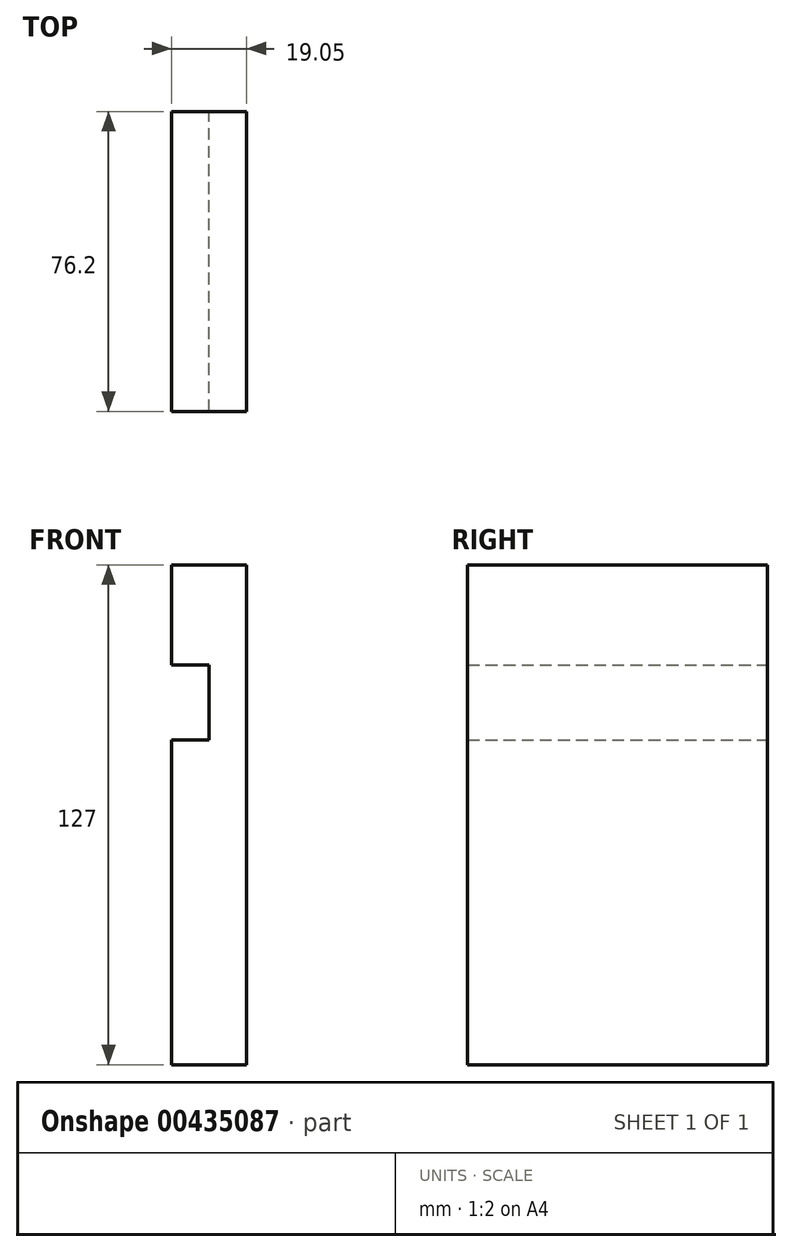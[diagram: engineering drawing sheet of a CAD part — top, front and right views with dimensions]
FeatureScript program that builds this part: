
annotation { "Feature Type Name" : "Feature", "Feature Type Description" : "" }
export const myFeature = defineFeature(function(context is Context, id is Id, definition is map)
    precondition{}
    {
        {
            var Q0;
            Q0=qCreatedBy(makeId("Front.planeOp"),FACE);
            var sketch = newSketch(context, id + "F0", { "sketchPlane" : qUnion([Q0])});
            skLineSegment(sketch, "E0", {"start": v(-26.54, 65.3) * mm, "end": v(-26.54, 39.9) * mm});
            skLineSegment(sketch, "E1", {"start": v(-17.02, 39.9) * mm, "end": v(-26.54, 39.9) * mm});
            skLineSegment(sketch, "E2", {"start": v(-17.02, 39.9) * mm, "end": v(-17.02, 20.86) * mm});
            skLineSegment(sketch, "E3", {"start": v(-17.02, 20.86) * mm, "end": v(-26.54, 20.86) * mm});
            skLineSegment(sketch, "E4", {"start": v(-26.54, 65.3) * mm, "end": v(-7.5, 65.3) * mm});
            skLineSegment(sketch, "E5", {"start": v(-7.5, 65.3) * mm, "end": v(-7.5, -61.7) * mm});
            skLineSegment(sketch, "E6", {"start": v(-7.5, -61.7) * mm, "end": v(-26.54, -61.7) * mm});
            skLineSegment(sketch, "E7", {"start": v(-26.54, -61.7) * mm, "end": v(-26.54, 20.86) * mm});
            skSolve(sketch);
        }
        {
            var Q0;
            Q0 = qSketchRegion(id + "F0", true);
            extrude(context, id + "F1", {"entities" : qUnion([Q0]), "depth" : 76.2 * mm});
        }
    });
